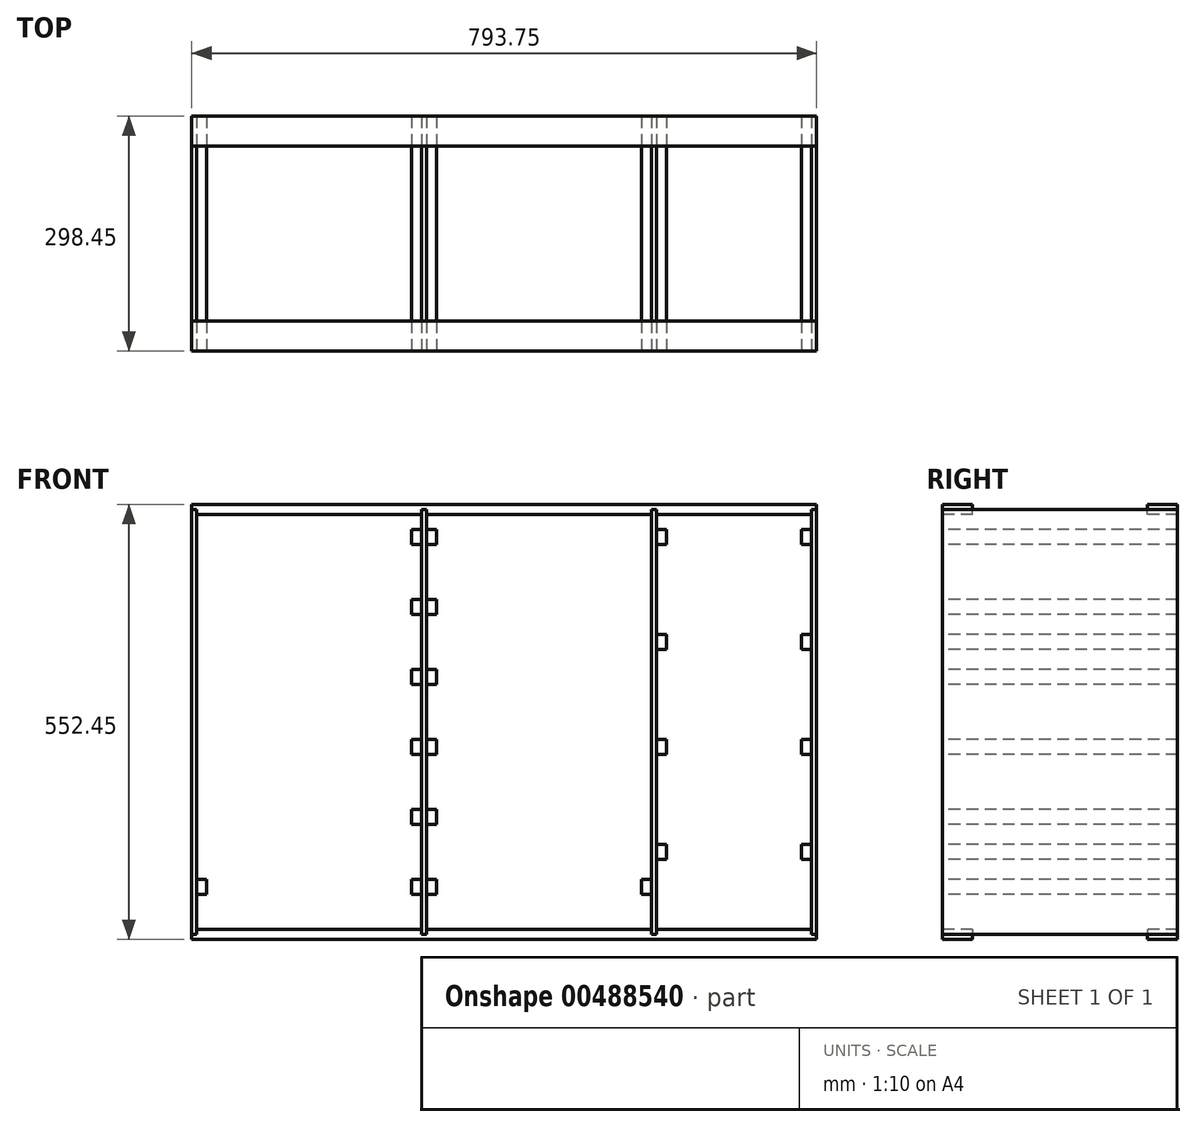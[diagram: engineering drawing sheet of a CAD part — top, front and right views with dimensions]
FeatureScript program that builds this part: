
annotation { "Feature Type Name" : "Feature", "Feature Type Description" : "" }
export const myFeature = defineFeature(function(context is Context, id is Id, definition is map)
    precondition{}
    {
        {
            var Q0;
            Q0=qCreatedBy(makeId("Front.planeOp"),FACE);
            var sketch = newSketch(context, id + "F0", { "sketchPlane" : qUnion([Q0])});
            skLineSegment(sketch, "E0", {"start": v(0, 0) * mm, "end": v(0, 6.35) * mm});
            skLineSegment(sketch, "E1", {"start": v(0, 6.35) * mm, "end": v(6.35, 6.35) * mm});
            skLineSegment(sketch, "E2", {"start": v(6.35, 6.35) * mm, "end": v(6.35, 12.7) * mm});
            skLineSegment(sketch, "E3", {"start": v(6.35, 12.7) * mm, "end": v(292.1, 12.7) * mm});
            skLineSegment(sketch, "E4", {"start": v(292.1, 12.7) * mm, "end": v(292.1, 6.35) * mm});
            skLineSegment(sketch, "E5", {"start": v(292.1, 6.35) * mm, "end": v(298.45, 6.35) * mm});
            skLineSegment(sketch, "E6", {"start": v(298.45, 6.35) * mm, "end": v(298.45, 12.7) * mm});
            skLineSegment(sketch, "E7", {"start": v(298.45, 12.7) * mm, "end": v(584.2, 12.7) * mm});
            skLineSegment(sketch, "E8", {"start": v(584.2, 12.7) * mm, "end": v(584.2, 6.35) * mm});
            skLineSegment(sketch, "E9", {"start": v(584.2, 6.35) * mm, "end": v(590.55, 6.35) * mm});
            skLineSegment(sketch, "E10", {"start": v(590.55, 6.35) * mm, "end": v(590.55, 12.7) * mm});
            skLineSegment(sketch, "E11", {"start": v(590.55, 12.7) * mm, "end": v(787.4, 12.7) * mm});
            skLineSegment(sketch, "E12", {"start": v(787.4, 12.7) * mm, "end": v(787.4, 6.35) * mm});
            skLineSegment(sketch, "E13", {"start": v(787.4, 6.35) * mm, "end": v(793.75, 6.35) * mm});
            skLineSegment(sketch, "E14", {"start": v(793.75, 6.35) * mm, "end": v(793.75, 0) * mm});
            skLineSegment(sketch, "E15", {"start": v(793.75, 0) * mm, "end": v(0, 0) * mm});
            skSolve(sketch);
        }
        {
            var Q0;
            Q0 = qSketchRegion(id + "F0", true);
            extrude(context, id + "F1", {"entities" : qUnion([Q0]), "oppositeDirection" : true, "depth" : 38.1 * mm});
        }
        {
            var Q0;
            Q0=makeQuery(id+"F1.opExtrude","SWEPT_BODY",BODY,{"disambiguationData":[OSD([sQuery(id+"F0.wireOp",EDGE,"E0"),sQuery(id+"F0.wireOp",EDGE,"E1"),sQuery(id+"F0.wireOp",EDGE,"E2"),sQuery(id+"F0.wireOp",EDGE,"E3"),sQuery(id+"F0.wireOp",EDGE,"E4"),sQuery(id+"F0.wireOp",EDGE,"E5"),sQuery(id+"F0.wireOp",EDGE,"E6"),sQuery(id+"F0.wireOp",EDGE,"E7"),sQuery(id+"F0.wireOp",EDGE,"E8"),sQuery(id+"F0.wireOp",EDGE,"E9"),sQuery(id+"F0.wireOp",EDGE,"E10"),sQuery(id+"F0.wireOp",EDGE,"E11"),sQuery(id+"F0.wireOp",EDGE,"E12"),sQuery(id+"F0.wireOp",EDGE,"E13"),sQuery(id+"F0.wireOp",EDGE,"E14"),sQuery(id+"F0.wireOp",EDGE,"E15")])]});
            var Q1;
            Q1=makeQuery(id+"F1.opExtrude","SWEPT_FACE",FACE,{"disambiguationData":[OSD([sQuery(id+"F0.wireOp",EDGE,"E3")])]});
            mirror(context, id + "F2", {"entities" : qUnion([Q0]), "mirrorPlane" : qUnion([Q1])});
        }
        {
            var Q0;
            Q0=makeQuery(id+"F2.opPattern","COPY",BODY,{"derivedFrom":makeQuery(id+"F1.opExtrude","SWEPT_BODY",BODY,{"disambiguationData":[OSD([sQuery(id+"F0.wireOp",EDGE,"E0"),sQuery(id+"F0.wireOp",EDGE,"E1"),sQuery(id+"F0.wireOp",EDGE,"E2"),sQuery(id+"F0.wireOp",EDGE,"E3"),sQuery(id+"F0.wireOp",EDGE,"E4"),sQuery(id+"F0.wireOp",EDGE,"E5"),sQuery(id+"F0.wireOp",EDGE,"E6"),sQuery(id+"F0.wireOp",EDGE,"E7"),sQuery(id+"F0.wireOp",EDGE,"E8"),sQuery(id+"F0.wireOp",EDGE,"E9"),sQuery(id+"F0.wireOp",EDGE,"E10"),sQuery(id+"F0.wireOp",EDGE,"E11"),sQuery(id+"F0.wireOp",EDGE,"E12"),sQuery(id+"F0.wireOp",EDGE,"E13"),sQuery(id+"F0.wireOp",EDGE,"E14"),sQuery(id+"F0.wireOp",EDGE,"E15")])]}),"instanceName":"1"});
            var Q1;
            Q1=makeQuery(id+"F2.opPattern","COPY",EDGE,{"derivedFrom":makeQuery(id+"F1.opExtrude","CAP_EDGE",EDGE,{"disambiguationData":[OSD([sQuery(id+"F0.wireOp",EDGE,"E2")])],"isStart":true}),"instanceName":"1"});
            var Q2;
            Q2=makeQuery(id+"F2.opPattern","COPY",EDGE,{"derivedFrom":makeQuery(id+"F1.opExtrude","CAP_EDGE",EDGE,{"disambiguationData":[OSD([sQuery(id+"F0.wireOp",EDGE,"E2")])],"isStart":true}),"instanceName":"1"});
            transform(context, id + "F3", {"entities" : qUnion([Q0]), "transformType" : TransformType.TRANSLATION_DISTANCE, "transformDirection" : qUnion([Q2]), "distance" : 527.05 * mm, "oppositeDirection" : true, "makeCopy" : false});
        }
        {
            var Q0;
            Q0=makeQuery(id+"F1.opExtrude","CAP_FACE",FACE,{"disambiguationData":[OSD([sQuery(id+"F0.wireOp",EDGE,"E0"),sQuery(id+"F0.wireOp",EDGE,"E1"),sQuery(id+"F0.wireOp",EDGE,"E2"),sQuery(id+"F0.wireOp",EDGE,"E3"),sQuery(id+"F0.wireOp",EDGE,"E4"),sQuery(id+"F0.wireOp",EDGE,"E5"),sQuery(id+"F0.wireOp",EDGE,"E6"),sQuery(id+"F0.wireOp",EDGE,"E7"),sQuery(id+"F0.wireOp",EDGE,"E8"),sQuery(id+"F0.wireOp",EDGE,"E9"),sQuery(id+"F0.wireOp",EDGE,"E10"),sQuery(id+"F0.wireOp",EDGE,"E11"),sQuery(id+"F0.wireOp",EDGE,"E12"),sQuery(id+"F0.wireOp",EDGE,"E13"),sQuery(id+"F0.wireOp",EDGE,"E14"),sQuery(id+"F0.wireOp",EDGE,"E15")])],"isStart":true});
            var sketch = newSketch(context, id + "F4", { "sketchPlane" : qUnion([Q0])});
            skLineSegment(sketch, "E16.bottom", {"start": v(0, 6.35) * mm, "end": v(6.35, 6.35) * mm});
            skLineSegment(sketch, "E16.top", {"start": v(0, 546.1) * mm, "end": v(6.35, 546.1) * mm});
            skLineSegment(sketch, "E16.left", {"start": v(0, 6.35) * mm, "end": v(0, 546.1) * mm});
            skLineSegment(sketch, "E16.right", {"start": v(6.35, 6.35) * mm, "end": v(6.35, 546.1) * mm});
            skLineSegment(sketch, "E17.0", {"start": v(6.35, 539.75) * mm, "end": v(292.1, 539.75) * mm});
            skLineSegment(sketch, "E18.bottom", {"start": v(584.2, 6.35) * mm, "end": v(590.55, 6.35) * mm});
            skLineSegment(sketch, "E18.top", {"start": v(584.2, 546.1) * mm, "end": v(590.55, 546.1) * mm});
            skLineSegment(sketch, "E18.left", {"start": v(584.2, 6.35) * mm, "end": v(584.2, 546.1) * mm});
            skLineSegment(sketch, "E18.right", {"start": v(590.55, 6.35) * mm, "end": v(590.55, 546.1) * mm});
            skLineSegment(sketch, "E19.bottom", {"start": v(787.4, 6.35) * mm, "end": v(793.75, 6.35) * mm});
            skLineSegment(sketch, "E19.top", {"start": v(787.4, 546.1) * mm, "end": v(793.75, 546.1) * mm});
            skLineSegment(sketch, "E19.left", {"start": v(787.4, 6.35) * mm, "end": v(787.4, 546.1) * mm});
            skLineSegment(sketch, "E19.right", {"start": v(793.75, 6.35) * mm, "end": v(793.75, 546.1) * mm});
            skLineSegment(sketch, "E20.bottom", {"start": v(292.1, 6.35) * mm, "end": v(298.45, 6.35) * mm});
            skLineSegment(sketch, "E20.top", {"start": v(292.1, 546.1) * mm, "end": v(298.45, 546.1) * mm});
            skLineSegment(sketch, "E20.left", {"start": v(292.1, 6.35) * mm, "end": v(292.1, 546.1) * mm});
            skLineSegment(sketch, "E20.right", {"start": v(298.45, 6.35) * mm, "end": v(298.45, 546.1) * mm});
            skLineSegment(sketch, "E21.bottom", {"start": v(6.35, 57.15) * mm, "end": v(19.05, 57.15) * mm});
            skLineSegment(sketch, "E21.top", {"start": v(6.35, 76.2) * mm, "end": v(19.05, 76.2) * mm});
            skLineSegment(sketch, "E21.left", {"start": v(6.35, 57.15) * mm, "end": v(6.35, 76.2) * mm});
            skLineSegment(sketch, "E21.right", {"start": v(19.05, 57.15) * mm, "end": v(19.05, 76.2) * mm});
            skLineSegment(sketch, "E22.bottom", {"start": v(292.1, 57.15) * mm, "end": v(279.4, 57.15) * mm});
            skLineSegment(sketch, "E22.top", {"start": v(292.1, 76.2) * mm, "end": v(279.4, 76.2) * mm});
            skLineSegment(sketch, "E22.left", {"start": v(292.1, 57.15) * mm, "end": v(292.1, 76.2) * mm});
            skLineSegment(sketch, "E22.right", {"start": v(279.4, 57.15) * mm, "end": v(279.4, 76.2) * mm});
            skLineSegment(sketch, "E23.bottom", {"start": v(298.45, 57.15) * mm, "end": v(311.15, 57.15) * mm});
            skLineSegment(sketch, "E23.top", {"start": v(298.45, 76.2) * mm, "end": v(311.15, 76.2) * mm});
            skLineSegment(sketch, "E23.left", {"start": v(298.45, 57.15) * mm, "end": v(298.45, 76.2) * mm});
            skLineSegment(sketch, "E23.right", {"start": v(311.15, 57.15) * mm, "end": v(311.15, 76.2) * mm});
            skLineSegment(sketch, "E24.bottom", {"start": v(584.2, 57.15) * mm, "end": v(571.5, 57.15) * mm});
            skLineSegment(sketch, "E24.top", {"start": v(584.2, 76.2) * mm, "end": v(571.5, 76.2) * mm});
            skLineSegment(sketch, "E24.left", {"start": v(584.2, 57.15) * mm, "end": v(584.2, 76.2) * mm});
            skLineSegment(sketch, "E24.right", {"start": v(571.5, 57.15) * mm, "end": v(571.5, 76.2) * mm});
            skLineSegment(sketch, "E25.bottom", {"start": v(590.55, 101.6) * mm, "end": v(603.25, 101.6) * mm});
            skLineSegment(sketch, "E25.top", {"start": v(590.55, 120.65) * mm, "end": v(603.25, 120.65) * mm});
            skLineSegment(sketch, "E25.left", {"start": v(590.55, 101.6) * mm, "end": v(590.55, 120.65) * mm});
            skLineSegment(sketch, "E25.right", {"start": v(603.25, 101.6) * mm, "end": v(603.25, 120.65) * mm});
            skLineSegment(sketch, "E26.bottom", {"start": v(787.4, 101.6) * mm, "end": v(774.7, 101.6) * mm});
            skLineSegment(sketch, "E26.top", {"start": v(787.4, 120.65) * mm, "end": v(774.7, 120.65) * mm});
            skLineSegment(sketch, "E26.left", {"start": v(787.4, 101.6) * mm, "end": v(787.4, 120.65) * mm});
            skLineSegment(sketch, "E26.right", {"start": v(774.7, 101.6) * mm, "end": v(774.7, 120.65) * mm});
            skLineSegment(sketch, "E27.0.1.0", {"start": v(584.2, 146.05) * mm, "end": v(584.2, 165.1) * mm});
            skLineSegment(sketch, "E27.0.1.1", {"start": v(6.35, 146.05) * mm, "end": v(6.35, 165.1) * mm});
            skLineSegment(sketch, "E27.0.1.2", {"start": v(279.4, 146.05) * mm, "end": v(279.4, 165.1) * mm});
            skLineSegment(sketch, "E27.0.1.3", {"start": v(311.15, 146.05) * mm, "end": v(311.15, 165.1) * mm});
            skLineSegment(sketch, "E27.0.1.4", {"start": v(19.05, 146.05) * mm, "end": v(19.05, 165.1) * mm});
            skLineSegment(sketch, "E27.0.1.5", {"start": v(298.45, 146.05) * mm, "end": v(298.45, 165.1) * mm});
            skLineSegment(sketch, "E27.0.1.6", {"start": v(571.5, 146.05) * mm, "end": v(571.5, 165.1) * mm});
            skLineSegment(sketch, "E27.0.1.7", {"start": v(292.1, 146.05) * mm, "end": v(292.1, 165.1) * mm});
            skLineSegment(sketch, "E27.0.1.8", {"start": v(584.2, 165.1) * mm, "end": v(571.5, 165.1) * mm});
            skLineSegment(sketch, "E27.0.1.9", {"start": v(6.35, 165.1) * mm, "end": v(19.05, 165.1) * mm});
            skLineSegment(sketch, "E27.0.1.10", {"start": v(584.2, 146.05) * mm, "end": v(571.5, 146.05) * mm});
            skLineSegment(sketch, "E27.0.1.11", {"start": v(6.35, 146.05) * mm, "end": v(19.05, 146.05) * mm});
            skLineSegment(sketch, "E27.0.1.12", {"start": v(298.45, 146.05) * mm, "end": v(311.15, 146.05) * mm});
            skLineSegment(sketch, "E27.0.1.13", {"start": v(292.1, 146.05) * mm, "end": v(279.4, 146.05) * mm});
            skLineSegment(sketch, "E27.0.1.14", {"start": v(292.1, 165.1) * mm, "end": v(279.4, 165.1) * mm});
            skLineSegment(sketch, "E27.0.1.15", {"start": v(298.45, 165.1) * mm, "end": v(311.15, 165.1) * mm});
            skLineSegment(sketch, "E27.0.2.0", {"start": v(584.2, 234.95) * mm, "end": v(584.2, 254) * mm});
            skLineSegment(sketch, "E27.0.2.1", {"start": v(6.35, 234.95) * mm, "end": v(6.35, 254) * mm});
            skLineSegment(sketch, "E27.0.2.2", {"start": v(279.4, 234.95) * mm, "end": v(279.4, 254) * mm});
            skLineSegment(sketch, "E27.0.2.3", {"start": v(311.15, 234.95) * mm, "end": v(311.15, 254) * mm});
            skLineSegment(sketch, "E27.0.2.4", {"start": v(19.05, 234.95) * mm, "end": v(19.05, 254) * mm});
            skLineSegment(sketch, "E27.0.2.5", {"start": v(298.45, 234.95) * mm, "end": v(298.45, 254) * mm});
            skLineSegment(sketch, "E27.0.2.6", {"start": v(571.5, 234.95) * mm, "end": v(571.5, 254) * mm});
            skLineSegment(sketch, "E27.0.2.7", {"start": v(292.1, 234.95) * mm, "end": v(292.1, 254) * mm});
            skLineSegment(sketch, "E27.0.2.8", {"start": v(584.2, 254) * mm, "end": v(571.5, 254) * mm});
            skLineSegment(sketch, "E27.0.2.9", {"start": v(6.35, 254) * mm, "end": v(19.05, 254) * mm});
            skLineSegment(sketch, "E27.0.2.10", {"start": v(584.2, 234.95) * mm, "end": v(571.5, 234.95) * mm});
            skLineSegment(sketch, "E27.0.2.11", {"start": v(6.35, 234.95) * mm, "end": v(19.05, 234.95) * mm});
            skLineSegment(sketch, "E27.0.2.12", {"start": v(298.45, 234.95) * mm, "end": v(311.15, 234.95) * mm});
            skLineSegment(sketch, "E27.0.2.13", {"start": v(292.1, 234.95) * mm, "end": v(279.4, 234.95) * mm});
            skLineSegment(sketch, "E27.0.2.14", {"start": v(292.1, 254) * mm, "end": v(279.4, 254) * mm});
            skLineSegment(sketch, "E27.0.2.15", {"start": v(298.45, 254) * mm, "end": v(311.15, 254) * mm});
            skLineSegment(sketch, "E27.0.3.0", {"start": v(584.2, 323.85) * mm, "end": v(584.2, 342.9) * mm});
            skLineSegment(sketch, "E27.0.3.1", {"start": v(6.35, 323.85) * mm, "end": v(6.35, 342.9) * mm});
            skLineSegment(sketch, "E27.0.3.2", {"start": v(279.4, 323.85) * mm, "end": v(279.4, 342.9) * mm});
            skLineSegment(sketch, "E27.0.3.3", {"start": v(311.15, 323.85) * mm, "end": v(311.15, 342.9) * mm});
            skLineSegment(sketch, "E27.0.3.4", {"start": v(19.05, 323.85) * mm, "end": v(19.05, 342.9) * mm});
            skLineSegment(sketch, "E27.0.3.5", {"start": v(298.45, 323.85) * mm, "end": v(298.45, 342.9) * mm});
            skLineSegment(sketch, "E27.0.3.6", {"start": v(571.5, 323.85) * mm, "end": v(571.5, 342.9) * mm});
            skLineSegment(sketch, "E27.0.3.7", {"start": v(292.1, 323.85) * mm, "end": v(292.1, 342.9) * mm});
            skLineSegment(sketch, "E27.0.3.8", {"start": v(584.2, 342.9) * mm, "end": v(571.5, 342.9) * mm});
            skLineSegment(sketch, "E27.0.3.9", {"start": v(6.35, 342.9) * mm, "end": v(19.05, 342.9) * mm});
            skLineSegment(sketch, "E27.0.3.10", {"start": v(584.2, 323.85) * mm, "end": v(571.5, 323.85) * mm});
            skLineSegment(sketch, "E27.0.3.11", {"start": v(6.35, 323.85) * mm, "end": v(19.05, 323.85) * mm});
            skLineSegment(sketch, "E27.0.3.12", {"start": v(298.45, 323.85) * mm, "end": v(311.15, 323.85) * mm});
            skLineSegment(sketch, "E27.0.3.13", {"start": v(292.1, 323.85) * mm, "end": v(279.4, 323.85) * mm});
            skLineSegment(sketch, "E27.0.3.14", {"start": v(292.1, 342.9) * mm, "end": v(279.4, 342.9) * mm});
            skLineSegment(sketch, "E27.0.3.15", {"start": v(298.45, 342.9) * mm, "end": v(311.15, 342.9) * mm});
            skLineSegment(sketch, "E27.0.4.0", {"start": v(584.2, 412.75) * mm, "end": v(584.2, 431.8) * mm});
            skLineSegment(sketch, "E27.0.4.1", {"start": v(6.35, 412.75) * mm, "end": v(6.35, 431.8) * mm});
            skLineSegment(sketch, "E27.0.4.2", {"start": v(279.4, 412.75) * mm, "end": v(279.4, 431.8) * mm});
            skLineSegment(sketch, "E27.0.4.3", {"start": v(311.15, 412.75) * mm, "end": v(311.15, 431.8) * mm});
            skLineSegment(sketch, "E27.0.4.4", {"start": v(19.05, 412.75) * mm, "end": v(19.05, 431.8) * mm});
            skLineSegment(sketch, "E27.0.4.5", {"start": v(298.45, 412.75) * mm, "end": v(298.45, 431.8) * mm});
            skLineSegment(sketch, "E27.0.4.6", {"start": v(571.5, 412.75) * mm, "end": v(571.5, 431.8) * mm});
            skLineSegment(sketch, "E27.0.4.7", {"start": v(292.1, 412.75) * mm, "end": v(292.1, 431.8) * mm});
            skLineSegment(sketch, "E27.0.4.8", {"start": v(584.2, 431.8) * mm, "end": v(571.5, 431.8) * mm});
            skLineSegment(sketch, "E27.0.4.9", {"start": v(6.35, 431.8) * mm, "end": v(19.05, 431.8) * mm});
            skLineSegment(sketch, "E27.0.4.10", {"start": v(584.2, 412.75) * mm, "end": v(571.5, 412.75) * mm});
            skLineSegment(sketch, "E27.0.4.11", {"start": v(6.35, 412.75) * mm, "end": v(19.05, 412.75) * mm});
            skLineSegment(sketch, "E27.0.4.12", {"start": v(298.45, 412.75) * mm, "end": v(311.15, 412.75) * mm});
            skLineSegment(sketch, "E27.0.4.13", {"start": v(292.1, 412.75) * mm, "end": v(279.4, 412.75) * mm});
            skLineSegment(sketch, "E27.0.4.14", {"start": v(292.1, 431.8) * mm, "end": v(279.4, 431.8) * mm});
            skLineSegment(sketch, "E27.0.4.15", {"start": v(298.45, 431.8) * mm, "end": v(311.15, 431.8) * mm});
            skLineSegment(sketch, "E27.0.5.0", {"start": v(584.2, 501.65) * mm, "end": v(584.2, 520.7) * mm});
            skLineSegment(sketch, "E27.0.5.1", {"start": v(6.35, 501.65) * mm, "end": v(6.35, 520.7) * mm});
            skLineSegment(sketch, "E27.0.5.2", {"start": v(279.4, 501.65) * mm, "end": v(279.4, 520.7) * mm});
            skLineSegment(sketch, "E27.0.5.3", {"start": v(311.15, 501.65) * mm, "end": v(311.15, 520.7) * mm});
            skLineSegment(sketch, "E27.0.5.4", {"start": v(19.05, 501.65) * mm, "end": v(19.05, 520.7) * mm});
            skLineSegment(sketch, "E27.0.5.5", {"start": v(298.45, 501.65) * mm, "end": v(298.45, 520.7) * mm});
            skLineSegment(sketch, "E27.0.5.6", {"start": v(571.5, 501.65) * mm, "end": v(571.5, 520.7) * mm});
            skLineSegment(sketch, "E27.0.5.7", {"start": v(292.1, 501.65) * mm, "end": v(292.1, 520.7) * mm});
            skLineSegment(sketch, "E27.0.5.8", {"start": v(584.2, 520.7) * mm, "end": v(571.5, 520.7) * mm});
            skLineSegment(sketch, "E27.0.5.9", {"start": v(6.35, 520.7) * mm, "end": v(19.05, 520.7) * mm});
            skLineSegment(sketch, "E27.0.5.10", {"start": v(584.2, 501.65) * mm, "end": v(571.5, 501.65) * mm});
            skLineSegment(sketch, "E27.0.5.11", {"start": v(6.35, 501.65) * mm, "end": v(19.05, 501.65) * mm});
            skLineSegment(sketch, "E27.0.5.12", {"start": v(298.45, 501.65) * mm, "end": v(311.15, 501.65) * mm});
            skLineSegment(sketch, "E27.0.5.13", {"start": v(292.1, 501.65) * mm, "end": v(279.4, 501.65) * mm});
            skLineSegment(sketch, "E27.0.5.14", {"start": v(292.1, 520.7) * mm, "end": v(279.4, 520.7) * mm});
            skLineSegment(sketch, "E27.0.5.15", {"start": v(298.45, 520.7) * mm, "end": v(311.15, 520.7) * mm});
            skLineSegment(sketch, "E27.direction1", {"start": v(6.35, 57.15) * mm, "end": v(31.75, 57.15) * mm, "construction": true});
            skLineSegment(sketch, "E27.direction2", {"start": v(6.35, 57.15) * mm, "end": v(6.35, 146.05) * mm, "construction": true});
            skLineSegment(sketch, "E28.0.1.0", {"start": v(590.55, 254) * mm, "end": v(603.25, 254) * mm});
            skLineSegment(sketch, "E28.0.1.1", {"start": v(590.55, 234.95) * mm, "end": v(603.25, 234.95) * mm});
            skLineSegment(sketch, "E28.0.1.2", {"start": v(603.25, 234.95) * mm, "end": v(603.25, 254) * mm});
            skLineSegment(sketch, "E28.0.1.3", {"start": v(590.55, 234.95) * mm, "end": v(590.55, 254) * mm});
            skLineSegment(sketch, "E28.0.1.4", {"start": v(787.4, 234.95) * mm, "end": v(774.7, 234.95) * mm});
            skLineSegment(sketch, "E28.0.1.5", {"start": v(787.4, 254) * mm, "end": v(774.7, 254) * mm});
            skLineSegment(sketch, "E28.0.1.6", {"start": v(787.4, 234.95) * mm, "end": v(787.4, 254) * mm});
            skLineSegment(sketch, "E28.0.1.7", {"start": v(774.7, 234.95) * mm, "end": v(774.7, 254) * mm});
            skLineSegment(sketch, "E28.0.2.0", {"start": v(590.55, 387.35) * mm, "end": v(603.25, 387.35) * mm});
            skLineSegment(sketch, "E28.0.2.1", {"start": v(590.55, 368.3) * mm, "end": v(603.25, 368.3) * mm});
            skLineSegment(sketch, "E28.0.2.2", {"start": v(603.25, 368.3) * mm, "end": v(603.25, 387.35) * mm});
            skLineSegment(sketch, "E28.0.2.3", {"start": v(590.55, 368.3) * mm, "end": v(590.55, 387.35) * mm});
            skLineSegment(sketch, "E28.0.2.4", {"start": v(787.4, 368.3) * mm, "end": v(774.7, 368.3) * mm});
            skLineSegment(sketch, "E28.0.2.5", {"start": v(787.4, 387.35) * mm, "end": v(774.7, 387.35) * mm});
            skLineSegment(sketch, "E28.0.2.6", {"start": v(787.4, 368.3) * mm, "end": v(787.4, 387.35) * mm});
            skLineSegment(sketch, "E28.0.2.7", {"start": v(774.7, 368.3) * mm, "end": v(774.7, 387.35) * mm});
            skLineSegment(sketch, "E28.0.3.0", {"start": v(590.55, 520.7) * mm, "end": v(603.25, 520.7) * mm});
            skLineSegment(sketch, "E28.0.3.1", {"start": v(590.55, 501.65) * mm, "end": v(603.25, 501.65) * mm});
            skLineSegment(sketch, "E28.0.3.2", {"start": v(603.25, 501.65) * mm, "end": v(603.25, 520.7) * mm});
            skLineSegment(sketch, "E28.0.3.3", {"start": v(590.55, 501.65) * mm, "end": v(590.55, 520.7) * mm});
            skLineSegment(sketch, "E28.0.3.4", {"start": v(787.4, 501.65) * mm, "end": v(774.7, 501.65) * mm});
            skLineSegment(sketch, "E28.0.3.5", {"start": v(787.4, 520.7) * mm, "end": v(774.7, 520.7) * mm});
            skLineSegment(sketch, "E28.0.3.6", {"start": v(787.4, 501.65) * mm, "end": v(787.4, 520.7) * mm});
            skLineSegment(sketch, "E28.0.3.7", {"start": v(774.7, 501.65) * mm, "end": v(774.7, 520.7) * mm});
            skLineSegment(sketch, "E28.direction1", {"start": v(590.55, 101.6) * mm, "end": v(615.95, 101.6) * mm, "construction": true});
            skLineSegment(sketch, "E28.direction2", {"start": v(590.55, 101.6) * mm, "end": v(590.55, 234.95) * mm, "construction": true});
            skSolve(sketch);
        }
        {
            var Q0;
            {var subQ7=sQuery(id+"F4.wireOp",EDGE,"E19.bottom");Q0=makeQuery(id+"F4.imprint","IMPRINT",FACE,{"disambiguationData":[TD([[makeQuery(id+"F4.imprint","IMPRINT",EDGE,{"derivedFrom":subQ7}),1.0]])]});}
            var Q1;
            {var subQ4=sQuery(id+"F4.wireOp",EDGE,"E16.bottom");Q1=makeQuery(id+"F4.imprint","IMPRINT",FACE,{"disambiguationData":[TD([[makeQuery(id+"F4.imprint","IMPRINT",EDGE,{"derivedFrom":subQ4}),1.0]])]});}
            var Q2;
            {var subQ7=sQuery(id+"F4.wireOp",EDGE,"E18.bottom");Q2=makeQuery(id+"F4.imprint","IMPRINT",FACE,{"disambiguationData":[TD([[makeQuery(id+"F4.imprint","IMPRINT",EDGE,{"derivedFrom":subQ7}),1.0]])]});}
            var Q3;
            {var subQ6=sQuery(id+"F4.wireOp",EDGE,"E20.bottom");Q3=makeQuery(id+"F4.imprint","IMPRINT",FACE,{"disambiguationData":[TD([[makeQuery(id+"F4.imprint","IMPRINT",EDGE,{"derivedFrom":subQ6}),1.0]])]});}
            extrude(context, id + "F5", {"entities" : qUnion([Q0, Q1, Q2, Q3]), "oppositeDirection" : true, "depth" : 298.45 * mm});
        }
        {
            var Q0;
            Q0=makeQuery(id+"F4.imprint","IMPRINT",FACE,{"disambiguationData":[TD([[makeQuery(id+"F4.imprint","IMPRINT",EDGE,{"derivedFrom":sQuery(id+"F4.wireOp",EDGE,"E27.0.5.1")}),-1.0]])]});
            var Q1;
            Q1=makeQuery(id+"F4.imprint","IMPRINT",FACE,{"disambiguationData":[TD([[makeQuery(id+"F4.imprint","IMPRINT",EDGE,{"derivedFrom":sQuery(id+"F4.wireOp",EDGE,"E27.0.4.1")}),-1.0]])]});
            var Q2;
            Q2=makeQuery(id+"F4.imprint","IMPRINT",FACE,{"disambiguationData":[TD([[makeQuery(id+"F4.imprint","IMPRINT",EDGE,{"derivedFrom":sQuery(id+"F4.wireOp",EDGE,"E27.0.3.1")}),-1.0]])]});
            var Q3;
            Q3=makeQuery(id+"F4.imprint","IMPRINT",FACE,{"disambiguationData":[TD([[makeQuery(id+"F4.imprint","IMPRINT",EDGE,{"derivedFrom":sQuery(id+"F4.wireOp",EDGE,"E27.0.2.1")}),-1.0]])]});
            var Q4;
            Q4=makeQuery(id+"F4.imprint","IMPRINT",FACE,{"disambiguationData":[TD([[makeQuery(id+"F4.imprint","IMPRINT",EDGE,{"derivedFrom":sQuery(id+"F4.wireOp",EDGE,"E27.0.1.1")}),-1.0]])]});
            var Q5;
            Q5=makeQuery(id+"F4.imprint","IMPRINT",FACE,{"disambiguationData":[TD([[makeQuery(id+"F4.imprint","IMPRINT",EDGE,{"derivedFrom":sQuery(id+"F4.wireOp",EDGE,"E21.bottom")}),1.0]])]});
            var Q6;
            Q6=makeQuery(id+"F4.imprint","IMPRINT",FACE,{"disambiguationData":[TD([[makeQuery(id+"F4.imprint","IMPRINT",EDGE,{"derivedFrom":sQuery(id+"F4.wireOp",EDGE,"E22.bottom")}),-1.0]])]});
            var Q7;
            Q7=makeQuery(id+"F4.imprint","IMPRINT",FACE,{"disambiguationData":[TD([[makeQuery(id+"F4.imprint","IMPRINT",EDGE,{"derivedFrom":sQuery(id+"F4.wireOp",EDGE,"E23.bottom")}),1.0]])]});
            var Q8;
            Q8=makeQuery(id+"F4.imprint","IMPRINT",FACE,{"disambiguationData":[TD([[makeQuery(id+"F4.imprint","IMPRINT",EDGE,{"derivedFrom":sQuery(id+"F4.wireOp",EDGE,"E27.0.1.2")}),-1.0]])]});
            var Q9;
            Q9=makeQuery(id+"F4.imprint","IMPRINT",FACE,{"disambiguationData":[TD([[makeQuery(id+"F4.imprint","IMPRINT",EDGE,{"derivedFrom":sQuery(id+"F4.wireOp",EDGE,"E27.0.1.3")}),1.0]])]});
            var Q10;
            Q10=makeQuery(id+"F4.imprint","IMPRINT",FACE,{"disambiguationData":[TD([[makeQuery(id+"F4.imprint","IMPRINT",EDGE,{"derivedFrom":sQuery(id+"F4.wireOp",EDGE,"E27.0.2.2")}),-1.0]])]});
            var Q11;
            Q11=makeQuery(id+"F4.imprint","IMPRINT",FACE,{"disambiguationData":[TD([[makeQuery(id+"F4.imprint","IMPRINT",EDGE,{"derivedFrom":sQuery(id+"F4.wireOp",EDGE,"E27.0.2.3")}),1.0]])]});
            var Q12;
            Q12=makeQuery(id+"F4.imprint","IMPRINT",FACE,{"disambiguationData":[TD([[makeQuery(id+"F4.imprint","IMPRINT",EDGE,{"derivedFrom":sQuery(id+"F4.wireOp",EDGE,"E27.0.3.3")}),1.0]])]});
            var Q13;
            Q13=makeQuery(id+"F4.imprint","IMPRINT",FACE,{"disambiguationData":[TD([[makeQuery(id+"F4.imprint","IMPRINT",EDGE,{"derivedFrom":sQuery(id+"F4.wireOp",EDGE,"E27.0.3.2")}),-1.0]])]});
            var Q14;
            Q14=makeQuery(id+"F4.imprint","IMPRINT",FACE,{"disambiguationData":[TD([[makeQuery(id+"F4.imprint","IMPRINT",EDGE,{"derivedFrom":sQuery(id+"F4.wireOp",EDGE,"E27.0.4.2")}),-1.0]])]});
            var Q15;
            Q15=makeQuery(id+"F4.imprint","IMPRINT",FACE,{"disambiguationData":[TD([[makeQuery(id+"F4.imprint","IMPRINT",EDGE,{"derivedFrom":sQuery(id+"F4.wireOp",EDGE,"E27.0.4.3")}),1.0]])]});
            var Q16;
            Q16=makeQuery(id+"F4.imprint","IMPRINT",FACE,{"disambiguationData":[TD([[makeQuery(id+"F4.imprint","IMPRINT",EDGE,{"derivedFrom":sQuery(id+"F4.wireOp",EDGE,"E27.0.5.2")}),-1.0]])]});
            var Q17;
            Q17=makeQuery(id+"F4.imprint","IMPRINT",FACE,{"disambiguationData":[TD([[makeQuery(id+"F4.imprint","IMPRINT",EDGE,{"derivedFrom":sQuery(id+"F4.wireOp",EDGE,"E27.0.5.3")}),1.0]])]});
            var Q18;
            Q18=makeQuery(id+"F4.imprint","IMPRINT",FACE,{"disambiguationData":[TD([[makeQuery(id+"F4.imprint","IMPRINT",EDGE,{"derivedFrom":sQuery(id+"F4.wireOp",EDGE,"E27.0.5.0")}),1.0]])]});
            var Q19;
            Q19=makeQuery(id+"F4.imprint","IMPRINT",FACE,{"disambiguationData":[TD([[makeQuery(id+"F4.imprint","IMPRINT",EDGE,{"derivedFrom":sQuery(id+"F4.wireOp",EDGE,"E28.0.3.0")}),-1.0]])]});
            var Q20;
            Q20=makeQuery(id+"F4.imprint","IMPRINT",FACE,{"disambiguationData":[TD([[makeQuery(id+"F4.imprint","IMPRINT",EDGE,{"derivedFrom":sQuery(id+"F4.wireOp",EDGE,"E27.0.4.0")}),1.0]])]});
            var Q21;
            Q21=makeQuery(id+"F4.imprint","IMPRINT",FACE,{"disambiguationData":[TD([[makeQuery(id+"F4.imprint","IMPRINT",EDGE,{"derivedFrom":sQuery(id+"F4.wireOp",EDGE,"E28.0.2.0")}),-1.0]])]});
            var Q22;
            Q22=makeQuery(id+"F4.imprint","IMPRINT",FACE,{"disambiguationData":[TD([[makeQuery(id+"F4.imprint","IMPRINT",EDGE,{"derivedFrom":sQuery(id+"F4.wireOp",EDGE,"E27.0.3.0")}),1.0]])]});
            var Q23;
            Q23=makeQuery(id+"F4.imprint","IMPRINT",FACE,{"disambiguationData":[TD([[makeQuery(id+"F4.imprint","IMPRINT",EDGE,{"derivedFrom":sQuery(id+"F4.wireOp",EDGE,"E28.0.1.0")}),-1.0]])]});
            var Q24;
            Q24=makeQuery(id+"F4.imprint","IMPRINT",FACE,{"disambiguationData":[TD([[makeQuery(id+"F4.imprint","IMPRINT",EDGE,{"derivedFrom":sQuery(id+"F4.wireOp",EDGE,"E28.0.3.4")}),-1.0]])]});
            var Q25;
            Q25=makeQuery(id+"F4.imprint","IMPRINT",FACE,{"disambiguationData":[TD([[makeQuery(id+"F4.imprint","IMPRINT",EDGE,{"derivedFrom":sQuery(id+"F4.wireOp",EDGE,"E28.0.2.4")}),-1.0]])]});
            var Q26;
            Q26=makeQuery(id+"F4.imprint","IMPRINT",FACE,{"disambiguationData":[TD([[makeQuery(id+"F4.imprint","IMPRINT",EDGE,{"derivedFrom":sQuery(id+"F4.wireOp",EDGE,"E28.0.1.4")}),-1.0]])]});
            var Q27;
            Q27=makeQuery(id+"F4.imprint","IMPRINT",FACE,{"disambiguationData":[TD([[makeQuery(id+"F4.imprint","IMPRINT",EDGE,{"derivedFrom":sQuery(id+"F4.wireOp",EDGE,"E26.bottom")}),-1.0]])]});
            var Q28;
            Q28=makeQuery(id+"F4.imprint","IMPRINT",FACE,{"disambiguationData":[TD([[makeQuery(id+"F4.imprint","IMPRINT",EDGE,{"derivedFrom":sQuery(id+"F4.wireOp",EDGE,"E25.bottom")}),1.0]])]});
            var Q29;
            Q29=makeQuery(id+"F4.imprint","IMPRINT",FACE,{"disambiguationData":[TD([[makeQuery(id+"F4.imprint","IMPRINT",EDGE,{"derivedFrom":sQuery(id+"F4.wireOp",EDGE,"E24.bottom")}),-1.0]])]});
            var Q30;
            Q30=makeQuery(id+"F4.imprint","IMPRINT",FACE,{"disambiguationData":[TD([[makeQuery(id+"F4.imprint","IMPRINT",EDGE,{"derivedFrom":sQuery(id+"F4.wireOp",EDGE,"E27.0.1.0")}),1.0]])]});
            var Q31;
            Q31=makeQuery(id+"F4.imprint","IMPRINT",FACE,{"disambiguationData":[TD([[makeQuery(id+"F4.imprint","IMPRINT",EDGE,{"derivedFrom":sQuery(id+"F4.wireOp",EDGE,"E27.0.2.0")}),1.0]])]});
            extrude(context, id + "F6", {"entities" : qUnion([Q0, Q1, Q2, Q3, Q4, Q5, Q6, Q7, Q8, Q9, Q10, Q11, Q12, Q13, Q14, Q15, Q16, Q17, Q18, Q19, Q20, Q21, Q22, Q23, Q24, Q25, Q26, Q27, Q28, Q29, Q30, Q31]), "oppositeDirection" : true, "depth" : 298.45 * mm});
        }
        {
            var Q0;
            Q0=makeQuery(id+"F2.opPattern","COPY",BODY,{"derivedFrom":makeQuery(id+"F1.opExtrude","SWEPT_BODY",BODY,{"disambiguationData":[OSD([sQuery(id+"F0.wireOp",EDGE,"E0"),sQuery(id+"F0.wireOp",EDGE,"E1"),sQuery(id+"F0.wireOp",EDGE,"E2"),sQuery(id+"F0.wireOp",EDGE,"E3"),sQuery(id+"F0.wireOp",EDGE,"E4"),sQuery(id+"F0.wireOp",EDGE,"E5"),sQuery(id+"F0.wireOp",EDGE,"E6"),sQuery(id+"F0.wireOp",EDGE,"E7"),sQuery(id+"F0.wireOp",EDGE,"E8"),sQuery(id+"F0.wireOp",EDGE,"E9"),sQuery(id+"F0.wireOp",EDGE,"E10"),sQuery(id+"F0.wireOp",EDGE,"E11"),sQuery(id+"F0.wireOp",EDGE,"E12"),sQuery(id+"F0.wireOp",EDGE,"E13"),sQuery(id+"F0.wireOp",EDGE,"E14"),sQuery(id+"F0.wireOp",EDGE,"E15")])]}),"instanceName":"1"});
            var Q1;
            Q1=makeQuery(id+"F1.opExtrude","SWEPT_BODY",BODY,{"disambiguationData":[OSD([sQuery(id+"F0.wireOp",EDGE,"E0"),sQuery(id+"F0.wireOp",EDGE,"E1"),sQuery(id+"F0.wireOp",EDGE,"E2"),sQuery(id+"F0.wireOp",EDGE,"E3"),sQuery(id+"F0.wireOp",EDGE,"E4"),sQuery(id+"F0.wireOp",EDGE,"E5"),sQuery(id+"F0.wireOp",EDGE,"E6"),sQuery(id+"F0.wireOp",EDGE,"E7"),sQuery(id+"F0.wireOp",EDGE,"E8"),sQuery(id+"F0.wireOp",EDGE,"E9"),sQuery(id+"F0.wireOp",EDGE,"E10"),sQuery(id+"F0.wireOp",EDGE,"E11"),sQuery(id+"F0.wireOp",EDGE,"E12"),sQuery(id+"F0.wireOp",EDGE,"E13"),sQuery(id+"F0.wireOp",EDGE,"E14"),sQuery(id+"F0.wireOp",EDGE,"E15")])]});
            var Q2;
            Q2=makeQuery(id+"F5.opExtrude","SWEPT_EDGE",EDGE,{"disambiguationData":[OSD([sQuery(id+"F4.wireOp",EDGE,"E16.bottom"),sQuery(id+"F4.wireOp",EDGE,"E16.right")])]});
            transform(context, id + "F7", {"entities" : qUnion([Q0, Q1]), "transformType" : TransformType.TRANSLATION_DISTANCE, "transformDirection" : qUnion([Q2]), "distance" : 260.35 * mm, "oppositeDirection" : true, "makeCopy" : true});
        }
    });
